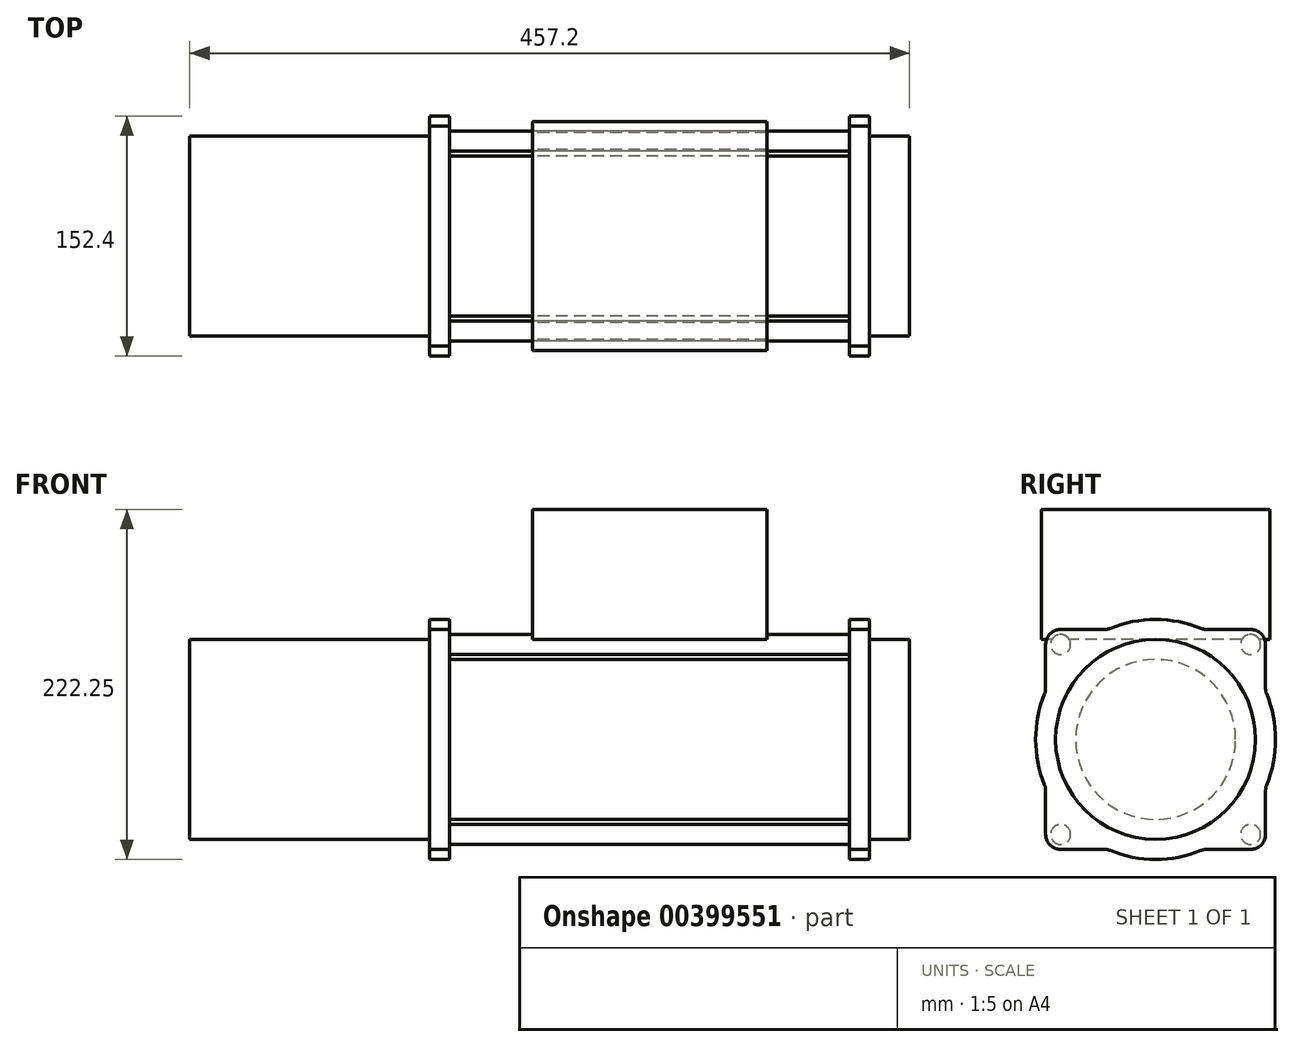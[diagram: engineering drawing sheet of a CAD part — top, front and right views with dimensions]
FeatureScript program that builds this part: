
annotation { "Feature Type Name" : "Feature", "Feature Type Description" : "" }
export const myFeature = defineFeature(function(context is Context, id is Id, definition is map)
    precondition{}
    {
        {
            var Q0;
            Q0=qCreatedBy(makeId("Right.planeOp"),FACE);
            var sketch = newSketch(context, id + "F0", { "sketchPlane" : qUnion([Q0])});
            skCircle(sketch, "E0", {"center": v(0, 0) * mm, "radius": 63.5 * mm});
            skSolve(sketch);
        }
        {
            var Q0;
            Q0=makeQuery(id+"F0.imprint","IMPRINT",FACE,{"disambiguationData":[TD([[makeQuery(id+"F0.imprint","IMPRINT",EDGE,{"derivedFrom":sQuery(id+"F0.wireOp",EDGE,"E0")}),1.0]])]});
            extrude(context, id + "F1", {"entities" : qUnion([Q0]), "depth" : 152.4 * mm});
        }
        {
            var Q0;
            Q0=makeQuery(id+"F1.opExtrude","CAP_FACE",FACE,{"disambiguationData":[OSD([sQuery(id+"F0.wireOp",EDGE,"E0")])],"isStart":false});
            var sketch = newSketch(context, id + "F2", { "sketchPlane" : qUnion([Q0])});
            skArc(sketch, "E1", {"start": v(-70.56, 28.78) * mm, "mid": v(-76.2, 0) * mm, "end": v(-70.56, -28.78) * mm});
            skLineSegment(sketch, "E2.bottom", {"start": v(60.33, 69.85) * mm, "end": v(32.38, 69.85) * mm});
            skLineSegment(sketch, "E2.top", {"start": v(60.33, -69.85) * mm, "end": v(32.38, -69.85) * mm});
            skLineSegment(sketch, "E2.left", {"start": v(69.85, 60.33) * mm, "end": v(69.85, 32.38) * mm});
            skLineSegment(sketch, "E2.right", {"start": v(-69.85, 60.33) * mm, "end": v(-69.85, 32.38) * mm});
            skLineSegment(sketch, "E3.trimOffspring", {"start": v(-32.38, 69.85) * mm, "end": v(-60.33, 69.85) * mm});
            skArc(sketch, "E4.trimOffspring", {"start": v(28.78, 70.56) * mm, "mid": v(0, 76.2) * mm, "end": v(-28.78, 70.56) * mm});
            skLineSegment(sketch, "E5.trimOffspring", {"start": v(69.85, -32.38) * mm, "end": v(69.85, -60.33) * mm});
            skArc(sketch, "E6.trimOffspring", {"start": v(70.56, -28.78) * mm, "mid": v(76.2, 0) * mm, "end": v(70.56, 28.78) * mm});
            skLineSegment(sketch, "E7.trimOffspring", {"start": v(-32.38, -69.85) * mm, "end": v(-60.33, -69.85) * mm});
            skArc(sketch, "E8.trimOffspring", {"start": v(-28.78, -70.56) * mm, "mid": v(0, -76.2) * mm, "end": v(28.78, -70.56) * mm});
            skLineSegment(sketch, "E9.trimOffspring", {"start": v(-69.85, -32.38) * mm, "end": v(-69.85, -60.33) * mm});
            skPoint(sketch, "E10.visualSharp", {"position": v(-69.85, 69.85) * mm});
            skArc(sketch, "E10.filletArc", {"start": v(-60.33, 69.85) * mm, "mid": v(-67.06, 67.06) * mm, "end": v(-69.85, 60.33) * mm});
            skPoint(sketch, "E11.visualSharp", {"position": v(-30.45, 69.85) * mm});
            skArc(sketch, "E11.filletArc", {"start": v(-32.38, 69.85) * mm, "mid": v(-30.55, 70.03) * mm, "end": v(-28.78, 70.56) * mm});
            skPoint(sketch, "E12.visualSharp", {"position": v(30.45, 69.85) * mm});
            skArc(sketch, "E12.filletArc", {"start": v(28.78, 70.56) * mm, "mid": v(30.55, 70.03) * mm, "end": v(32.38, 69.85) * mm});
            skPoint(sketch, "E13.visualSharp", {"position": v(69.85, 69.85) * mm});
            skArc(sketch, "E13.filletArc", {"start": v(69.85, 60.33) * mm, "mid": v(67.06, 67.06) * mm, "end": v(60.33, 69.85) * mm});
            skPoint(sketch, "E14.visualSharp", {"position": v(69.85, 30.45) * mm});
            skArc(sketch, "E14.filletArc", {"start": v(69.85, 32.38) * mm, "mid": v(70.03, 30.55) * mm, "end": v(70.56, 28.78) * mm});
            skPoint(sketch, "E15.visualSharp", {"position": v(69.85, -30.45) * mm});
            skArc(sketch, "E15.filletArc", {"start": v(70.56, -28.78) * mm, "mid": v(70.03, -30.55) * mm, "end": v(69.85, -32.38) * mm});
            skPoint(sketch, "E16.visualSharp", {"position": v(69.85, -69.85) * mm});
            skArc(sketch, "E16.filletArc", {"start": v(60.33, -69.85) * mm, "mid": v(67.06, -67.06) * mm, "end": v(69.85, -60.33) * mm});
            skPoint(sketch, "E17.visualSharp", {"position": v(30.45, -69.85) * mm});
            skArc(sketch, "E17.filletArc", {"start": v(32.38, -69.85) * mm, "mid": v(30.55, -70.03) * mm, "end": v(28.78, -70.56) * mm});
            skPoint(sketch, "E18.visualSharp", {"position": v(-30.45, -69.85) * mm});
            skArc(sketch, "E18.filletArc", {"start": v(-28.78, -70.56) * mm, "mid": v(-30.55, -70.03) * mm, "end": v(-32.38, -69.85) * mm});
            skPoint(sketch, "E19.visualSharp", {"position": v(-69.85, -69.85) * mm});
            skArc(sketch, "E19.filletArc", {"start": v(-69.85, -60.33) * mm, "mid": v(-67.06, -67.06) * mm, "end": v(-60.33, -69.85) * mm});
            skPoint(sketch, "E20.visualSharp", {"position": v(-69.85, -30.45) * mm});
            skArc(sketch, "E20.filletArc", {"start": v(-69.85, -32.38) * mm, "mid": v(-70.03, -30.55) * mm, "end": v(-70.56, -28.78) * mm});
            skPoint(sketch, "E21.visualSharp", {"position": v(-69.85, 30.45) * mm});
            skArc(sketch, "E21.filletArc", {"start": v(-70.56, 28.78) * mm, "mid": v(-70.03, 30.55) * mm, "end": v(-69.85, 32.38) * mm});
            skSolve(sketch);
        }
        {
            var Q0;
            Q0=makeQuery(id+"F2.imprint","IMPRINT",FACE,{"disambiguationData":[TD([[makeQuery(id+"F2.imprint","IMPRINT",EDGE,{"derivedFrom":sQuery(id+"F2.wireOp",EDGE,"E1")}),1.0]])]});
            var Q1;
            Q1=makeQuery(id+"F2.imprint","IMPRINT",FACE,{"disambiguationData":[TD([[makeQuery(id+"F2.imprint","IMPRINT",EDGE,{"derivedFrom":makeQuery(id+"F1.opExtrude","CAP_EDGE",EDGE,{"disambiguationData":[OSD([sQuery(id+"F0.wireOp",EDGE,"E0")])],"isStart":false})}),1.0]])]});
            extrude(context, id + "F3", {"entities" : qUnion([Q0, Q1]), "operationType" : NewBodyOperationType.ADD, "depth" : 12.7 * mm});
        }
        {
            var Q0;
            Q0=makeQuery(id+"F3.opExtrude","CAP_FACE",FACE,{"disambiguationData":[OSD([sQuery(id+"F2.wireOp",EDGE,"E1"),sQuery(id+"F2.wireOp",EDGE,"E2.bottom"),sQuery(id+"F2.wireOp",EDGE,"E2.top"),sQuery(id+"F2.wireOp",EDGE,"E2.left"),sQuery(id+"F2.wireOp",EDGE,"E2.right"),sQuery(id+"F2.wireOp",EDGE,"E3.trimOffspring"),sQuery(id+"F2.wireOp",EDGE,"E4.trimOffspring"),sQuery(id+"F2.wireOp",EDGE,"E5.trimOffspring"),sQuery(id+"F2.wireOp",EDGE,"E6.trimOffspring"),sQuery(id+"F2.wireOp",EDGE,"E7.trimOffspring"),sQuery(id+"F2.wireOp",EDGE,"E8.trimOffspring"),sQuery(id+"F2.wireOp",EDGE,"E9.trimOffspring"),sQuery(id+"F2.wireOp",EDGE,"E10.filletArc"),sQuery(id+"F2.wireOp",EDGE,"E11.filletArc"),sQuery(id+"F2.wireOp",EDGE,"E12.filletArc"),sQuery(id+"F2.wireOp",EDGE,"E13.filletArc"),sQuery(id+"F2.wireOp",EDGE,"E14.filletArc"),sQuery(id+"F2.wireOp",EDGE,"E15.filletArc"),sQuery(id+"F2.wireOp",EDGE,"E16.filletArc"),sQuery(id+"F2.wireOp",EDGE,"E17.filletArc"),sQuery(id+"F2.wireOp",EDGE,"E18.filletArc"),sQuery(id+"F2.wireOp",EDGE,"E19.filletArc"),sQuery(id+"F2.wireOp",EDGE,"E20.filletArc"),sQuery(id+"F2.wireOp",EDGE,"E21.filletArc")])],"isStart":false});
            var sketch = newSketch(context, id + "F4", { "sketchPlane" : qUnion([Q0])});
            skCircle(sketch, "E22", {"center": v(-60.33, 60.33) * mm, "radius": 6.35 * mm});
            skCircle(sketch, "E23", {"center": v(60.33, 60.33) * mm, "radius": 6.35 * mm});
            skCircle(sketch, "E24", {"center": v(60.33, -60.33) * mm, "radius": 6.35 * mm});
            skCircle(sketch, "E25", {"center": v(-60.33, -60.33) * mm, "radius": 6.35 * mm});
            skCircle(sketch, "E26", {"center": v(0, 0) * mm, "radius": 50.8 * mm});
            skSolve(sketch);
        }
        {
            var Q0;
            Q0=makeQuery(id+"F4.imprint","IMPRINT",FACE,{"disambiguationData":[TD([[makeQuery(id+"F4.imprint","IMPRINT",EDGE,{"derivedFrom":sQuery(id+"F4.wireOp",EDGE,"E26")}),1.0]])]});
            var Q1;
            Q1=makeQuery(id+"F4.imprint","IMPRINT",FACE,{"disambiguationData":[TD([[makeQuery(id+"F4.imprint","IMPRINT",EDGE,{"derivedFrom":sQuery(id+"F4.wireOp",EDGE,"E23")}),1.0]])]});
            var Q2;
            Q2=makeQuery(id+"F4.imprint","IMPRINT",FACE,{"disambiguationData":[TD([[makeQuery(id+"F4.imprint","IMPRINT",EDGE,{"derivedFrom":sQuery(id+"F4.wireOp",EDGE,"E24")}),1.0]])]});
            var Q3;
            Q3=makeQuery(id+"F4.imprint","IMPRINT",FACE,{"disambiguationData":[TD([[makeQuery(id+"F4.imprint","IMPRINT",EDGE,{"derivedFrom":sQuery(id+"F4.wireOp",EDGE,"E25")}),1.0]])]});
            var Q4;
            Q4=makeQuery(id+"F4.imprint","IMPRINT",FACE,{"disambiguationData":[TD([[makeQuery(id+"F4.imprint","IMPRINT",EDGE,{"derivedFrom":sQuery(id+"F4.wireOp",EDGE,"E22")}),1.0]])]});
            extrude(context, id + "F5", {"entities" : qUnion([Q0, Q1, Q2, Q3, Q4]), "operationType" : NewBodyOperationType.ADD, "depth" : 254 * mm});
        }
        {
            var Q0;
            Q0=makeQuery(id+"F5.opExtrude","CAP_FACE",FACE,{"disambiguationData":[OSD([sQuery(id+"F4.wireOp",EDGE,"E26")])],"isStart":false});
            var sketch = newSketch(context, id + "F6", { "sketchPlane" : qUnion([Q0])});
            skArc(sketch, "E27", {"start": v(-70.56, 28.78) * mm, "mid": v(-76.2, 0) * mm, "end": v(-70.56, -28.78) * mm});
            skLineSegment(sketch, "E28.bottom", {"start": v(60.33, 69.85) * mm, "end": v(32.38, 69.85) * mm});
            skLineSegment(sketch, "E28.top", {"start": v(60.33, -69.85) * mm, "end": v(32.38, -69.85) * mm});
            skLineSegment(sketch, "E28.left", {"start": v(69.85, 60.33) * mm, "end": v(69.85, 32.38) * mm});
            skLineSegment(sketch, "E28.right", {"start": v(-69.85, 60.33) * mm, "end": v(-69.85, 32.38) * mm});
            skLineSegment(sketch, "E29.trimOffspring", {"start": v(-32.38, 69.85) * mm, "end": v(-60.33, 69.85) * mm});
            skArc(sketch, "E30.trimOffspring", {"start": v(28.78, 70.56) * mm, "mid": v(0, 76.2) * mm, "end": v(-28.78, 70.56) * mm});
            skLineSegment(sketch, "E31.trimOffspring", {"start": v(69.85, -32.38) * mm, "end": v(69.85, -60.33) * mm});
            skArc(sketch, "E32.trimOffspring", {"start": v(70.56, -28.78) * mm, "mid": v(76.2, 0) * mm, "end": v(70.56, 28.78) * mm});
            skLineSegment(sketch, "E33.trimOffspring", {"start": v(-32.38, -69.85) * mm, "end": v(-60.33, -69.85) * mm});
            skArc(sketch, "E34.trimOffspring", {"start": v(-28.78, -70.56) * mm, "mid": v(0, -76.2) * mm, "end": v(28.78, -70.56) * mm});
            skLineSegment(sketch, "E35.trimOffspring", {"start": v(-69.85, -32.38) * mm, "end": v(-69.85, -60.33) * mm});
            skPoint(sketch, "E36.visualSharp", {"position": v(-69.85, 69.85) * mm});
            skArc(sketch, "E36.filletArc", {"start": v(-60.33, 69.85) * mm, "mid": v(-67.06, 67.06) * mm, "end": v(-69.85, 60.33) * mm});
            skPoint(sketch, "E37.visualSharp", {"position": v(-30.45, 69.85) * mm});
            skArc(sketch, "E37.filletArc", {"start": v(-32.38, 69.85) * mm, "mid": v(-30.55, 70.03) * mm, "end": v(-28.78, 70.56) * mm});
            skPoint(sketch, "E38.visualSharp", {"position": v(30.45, 69.85) * mm});
            skArc(sketch, "E38.filletArc", {"start": v(28.78, 70.56) * mm, "mid": v(30.55, 70.03) * mm, "end": v(32.38, 69.85) * mm});
            skPoint(sketch, "E39.visualSharp", {"position": v(69.85, 69.85) * mm});
            skArc(sketch, "E39.filletArc", {"start": v(69.85, 60.33) * mm, "mid": v(67.06, 67.06) * mm, "end": v(60.33, 69.85) * mm});
            skPoint(sketch, "E40.visualSharp", {"position": v(69.85, 30.45) * mm});
            skArc(sketch, "E40.filletArc", {"start": v(69.85, 32.38) * mm, "mid": v(70.03, 30.55) * mm, "end": v(70.56, 28.78) * mm});
            skPoint(sketch, "E41.visualSharp", {"position": v(69.85, -30.45) * mm});
            skArc(sketch, "E41.filletArc", {"start": v(70.56, -28.78) * mm, "mid": v(70.03, -30.55) * mm, "end": v(69.85, -32.38) * mm});
            skPoint(sketch, "E42.visualSharp", {"position": v(69.85, -69.85) * mm});
            skArc(sketch, "E42.filletArc", {"start": v(60.33, -69.85) * mm, "mid": v(67.06, -67.06) * mm, "end": v(69.85, -60.33) * mm});
            skPoint(sketch, "E43.visualSharp", {"position": v(30.45, -69.85) * mm});
            skArc(sketch, "E43.filletArc", {"start": v(32.38, -69.85) * mm, "mid": v(30.55, -70.03) * mm, "end": v(28.78, -70.56) * mm});
            skPoint(sketch, "E44.visualSharp", {"position": v(-30.45, -69.85) * mm});
            skArc(sketch, "E44.filletArc", {"start": v(-28.78, -70.56) * mm, "mid": v(-30.55, -70.03) * mm, "end": v(-32.38, -69.85) * mm});
            skPoint(sketch, "E45.visualSharp", {"position": v(-69.85, -69.85) * mm});
            skArc(sketch, "E45.filletArc", {"start": v(-69.85, -60.33) * mm, "mid": v(-67.06, -67.06) * mm, "end": v(-60.33, -69.85) * mm});
            skPoint(sketch, "E46.visualSharp", {"position": v(-69.85, -30.45) * mm});
            skArc(sketch, "E46.filletArc", {"start": v(-69.85, -32.38) * mm, "mid": v(-70.03, -30.55) * mm, "end": v(-70.56, -28.78) * mm});
            skPoint(sketch, "E47.visualSharp", {"position": v(-69.85, 30.45) * mm});
            skArc(sketch, "E47.filletArc", {"start": v(-70.56, 28.78) * mm, "mid": v(-70.03, 30.55) * mm, "end": v(-69.85, 32.38) * mm});
            skSolve(sketch);
        }
        {
            var Q0;
            Q0=makeQuery(id+"F6.imprint","IMPRINT",FACE,{"disambiguationData":[TD([[makeQuery(id+"F6.imprint","IMPRINT",EDGE,{"derivedFrom":sQuery(id+"F6.wireOp",EDGE,"E27")}),1.0]])]});
            var Q1;
            Q1=makeQuery(id+"F6.imprint","IMPRINT",FACE,{"disambiguationData":[TD([[makeQuery(id+"F6.imprint","IMPRINT",EDGE,{"derivedFrom":makeQuery(id+"F5.opExtrude","CAP_EDGE",EDGE,{"disambiguationData":[OSD([sQuery(id+"F4.wireOp",EDGE,"E26")])],"isStart":false})}),1.0]])]});
            extrude(context, id + "F7", {"entities" : qUnion([Q0, Q1]), "operationType" : NewBodyOperationType.ADD, "depth" : 12.7 * mm});
        }
        {
            var Q0;
            Q0=makeQuery(id+"F3.opExtrude","SWEPT_FACE",FACE,{"disambiguationData":[OSD([sQuery(id+"F2.wireOp",EDGE,"E3.trimOffspring")])]});
            var sketch = newSketch(context, id + "F8", { "sketchPlane" : qUnion([Q0])});
            skLineSegment(sketch, "E48.0", {"start": v(165.1, 28.78) * mm, "end": v(165.1, -28.78) * mm});
            skLineSegment(sketch, "E48.1", {"start": v(419.1, 28.78) * mm, "end": v(419.1, -28.78) * mm});
            skLineSegment(sketch, "E49", {"start": v(165.1, 0) * mm, "end": v(419.1, 0) * mm});
            skLineSegment(sketch, "E50.bottom", {"start": v(366.47, 72.56) * mm, "end": v(217.73, 72.56) * mm});
            skLineSegment(sketch, "E50.top", {"start": v(366.47, -72.56) * mm, "end": v(217.73, -72.56) * mm});
            skLineSegment(sketch, "E50.left", {"start": v(366.47, 72.56) * mm, "end": v(366.47, -72.56) * mm});
            skLineSegment(sketch, "E50.right", {"start": v(217.73, 72.56) * mm, "end": v(217.73, -72.56) * mm});
            skPoint(sketch, "E50.middle", {"position": v(292.1, 0) * mm});
            skSolve(sketch);
        }
        {
            var Q0;
            {var subQ5=sQuery(id+"F8.wireOp",EDGE,"E50.bottom");Q0=makeQuery(id+"F8.imprint","IMPRINT",FACE,{"disambiguationData":[TD([[makeQuery(id+"F8.imprint","IMPRINT",EDGE,{"derivedFrom":subQ5}),1.0]])]});}
            var Q1;
            {var subQ5=sQuery(id+"F8.wireOp",EDGE,"E50.top");Q1=makeQuery(id+"F8.imprint","IMPRINT",FACE,{"disambiguationData":[TD([[makeQuery(id+"F8.imprint","IMPRINT",EDGE,{"derivedFrom":subQ5}),-1.0]])]});}
            extrude(context, id + "F9", {"entities" : qUnion([Q0, Q1]), "operationType" : NewBodyOperationType.ADD, "depth" : 76.2 * mm, "hasSecondDirection" : true, "secondDirectionOppositeDirection" : true, "secondDirectionDepth" : 6.35 * mm});
        }
        {
            var Q0;
            Q0=makeQuery(id+"F7.opExtrude","CAP_FACE",FACE,{"disambiguationData":[OSD([sQuery(id+"F6.wireOp",EDGE,"E27"),sQuery(id+"F6.wireOp",EDGE,"E28.bottom"),sQuery(id+"F6.wireOp",EDGE,"E28.top"),sQuery(id+"F6.wireOp",EDGE,"E28.left"),sQuery(id+"F6.wireOp",EDGE,"E28.right"),sQuery(id+"F6.wireOp",EDGE,"E29.trimOffspring"),sQuery(id+"F6.wireOp",EDGE,"E30.trimOffspring"),sQuery(id+"F6.wireOp",EDGE,"E31.trimOffspring"),sQuery(id+"F6.wireOp",EDGE,"E32.trimOffspring"),sQuery(id+"F6.wireOp",EDGE,"E33.trimOffspring"),sQuery(id+"F6.wireOp",EDGE,"E34.trimOffspring"),sQuery(id+"F6.wireOp",EDGE,"E35.trimOffspring"),sQuery(id+"F6.wireOp",EDGE,"E36.filletArc"),sQuery(id+"F6.wireOp",EDGE,"E37.filletArc"),sQuery(id+"F6.wireOp",EDGE,"E38.filletArc"),sQuery(id+"F6.wireOp",EDGE,"E39.filletArc"),sQuery(id+"F6.wireOp",EDGE,"E40.filletArc"),sQuery(id+"F6.wireOp",EDGE,"E41.filletArc"),sQuery(id+"F6.wireOp",EDGE,"E42.filletArc"),sQuery(id+"F6.wireOp",EDGE,"E43.filletArc"),sQuery(id+"F6.wireOp",EDGE,"E44.filletArc"),sQuery(id+"F6.wireOp",EDGE,"E45.filletArc"),sQuery(id+"F6.wireOp",EDGE,"E46.filletArc"),sQuery(id+"F6.wireOp",EDGE,"E47.filletArc")])],"isStart":false});
            var sketch = newSketch(context, id + "F10", { "sketchPlane" : qUnion([Q0])});
            skCircle(sketch, "E51", {"center": v(0, 0) * mm, "radius": 63.5 * mm});
            skSolve(sketch);
        }
        {
            var Q0;
            Q0=makeQuery(id+"F10.imprint","IMPRINT",FACE,{"disambiguationData":[TD([[makeQuery(id+"F10.imprint","IMPRINT",EDGE,{"derivedFrom":sQuery(id+"F10.wireOp",EDGE,"E51")}),1.0]])]});
            extrude(context, id + "F11", {"entities" : qUnion([Q0]), "operationType" : NewBodyOperationType.ADD, "depth" : 25.4 * mm});
        }
    });
